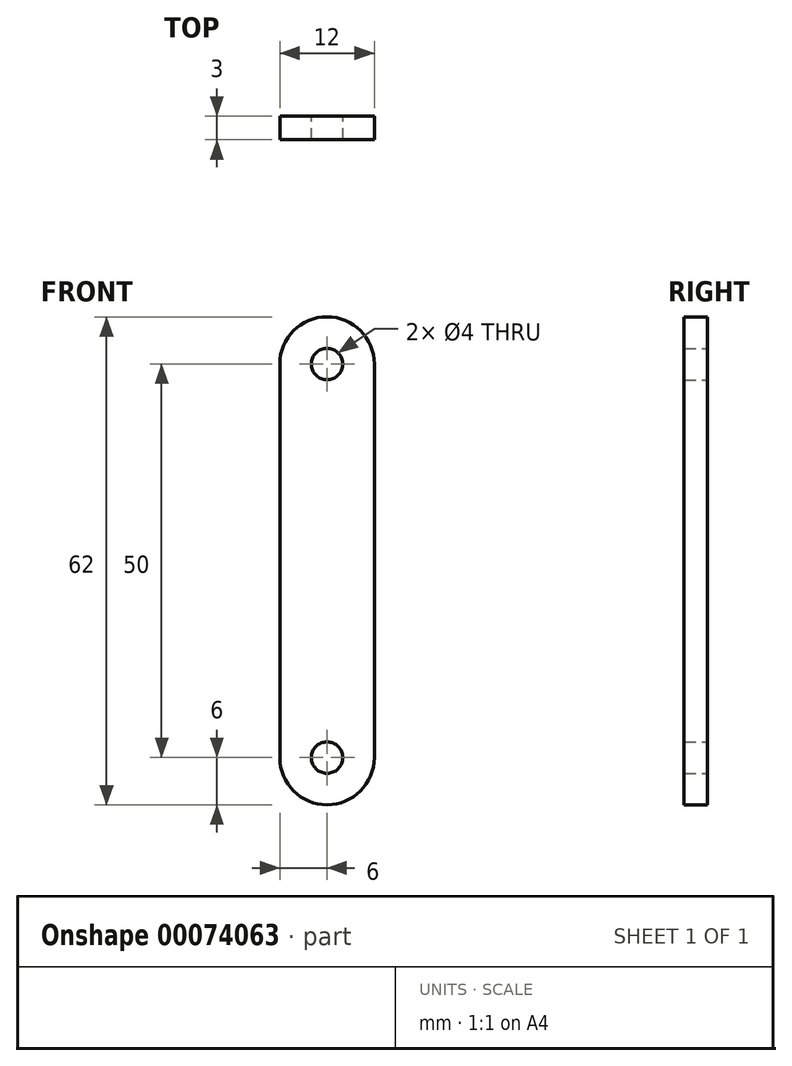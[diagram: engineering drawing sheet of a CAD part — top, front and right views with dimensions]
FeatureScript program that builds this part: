
annotation { "Feature Type Name" : "Feature", "Feature Type Description" : "" }
export const myFeature = defineFeature(function(context is Context, id is Id, definition is map)
    precondition{}
    {
        {
            var Q0;
            Q0=qCreatedBy(makeId("Front.planeOp"),FACE);
            var sketch = newSketch(context, id + "F0", { "sketchPlane" : qUnion([Q0])});
            skCircle(sketch, "E0", {"center": v(0, 0) * mm, "radius": 6 * mm});
            skCircle(sketch, "E1", {"center": v(0, -50) * mm, "radius": 6 * mm});
            skCircle(sketch, "E2", {"center": v(0, 0) * mm, "radius": 2 * mm});
            skCircle(sketch, "E3", {"center": v(0, -50) * mm, "radius": 2 * mm});
            skLineSegment(sketch, "E4", {"start": v(-6, 0) * mm, "end": v(-6, -50) * mm});
            skLineSegment(sketch, "E5", {"start": v(-6, -50) * mm, "end": v(6, -50) * mm});
            skLineSegment(sketch, "E6", {"start": v(6, -50) * mm, "end": v(6, 0) * mm});
            skLineSegment(sketch, "E7", {"start": v(6, 0) * mm, "end": v(-6, 0) * mm});
            skSolve(sketch);
        }
        {
            var Q0;
            Q0=qSketchRegion(id+"F0",true);
            extrude(context, id + "F1", {"entities" : qUnion([Q0]), "depth" : 3 * mm});
        }
    });
